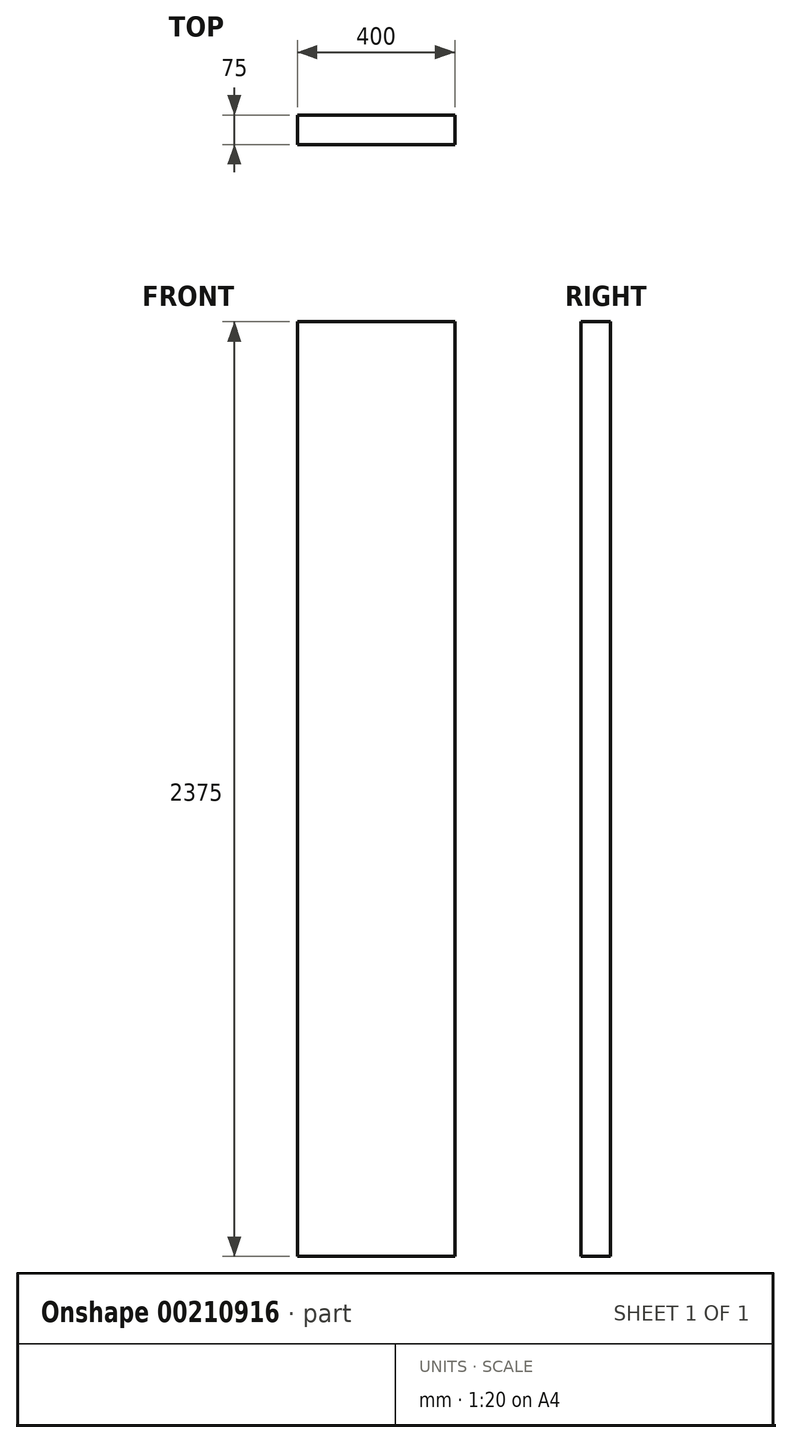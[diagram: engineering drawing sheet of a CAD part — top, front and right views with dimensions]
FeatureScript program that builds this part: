
annotation { "Feature Type Name" : "Feature", "Feature Type Description" : "" }
export const myFeature = defineFeature(function(context is Context, id is Id, definition is map)
    precondition{}
    {
        {
            var Q0;
            Q0=qCreatedBy(makeId("Front.planeOp"),FACE);
            var sketch = newSketch(context, id + "F0", { "sketchPlane" : qUnion([Q0])});
            skLineSegment(sketch, "E0.bottom", {"start": v(0, 0) * mm, "end": v(400, 0) * mm});
            skLineSegment(sketch, "E0.right", {"start": v(400, 0) * mm, "end": v(400, 2375) * mm});
            skLineSegment(sketch, "E1", {"start": v(0, 2375) * mm, "end": v(400, 2375) * mm});
            skLineSegment(sketch, "E2", {"start": v(0, 0) * mm, "end": v(0, 2375) * mm});
            skSolve(sketch);
        }
        {
            var Q0;
            Q0=makeQuery(id+"F0.imprint","IMPRINT",FACE,{"disambiguationData":[TD([[makeQuery(id+"F0.imprint","IMPRINT",EDGE,{"derivedFrom":sQuery(id+"F0.wireOp",EDGE,"E0.bottom")}),1.0]])]});
            extrude(context, id + "F1", {"entities" : qUnion([Q0]), "depth" : 75 * mm});
        }
    });
